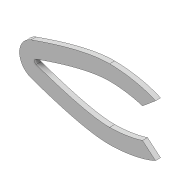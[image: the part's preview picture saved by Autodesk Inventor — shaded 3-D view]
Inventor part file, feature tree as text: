
AUTODESK INVENTOR PART (.ipt)
format: ipt  version: 2022 (Build 260153000, 153)  size: 121,856 bytes
history: native  units: mm
features: extrude x1, sketch x1
ambient origin geometry x8: Origin, YZ Plane, XZ Plane, XY Plane, X Axis, Y Axis, Z Axis, Center Point
bodies: Solid1 (feature_tree)
feature tree (2):
  extrude  "Extrusion1"  Depth=6.981317mm
  sketch  "Sketch1"  dims[d14=3.0mm d15=6.981317mm d16=6.981317mm d17=5.0mm d18=1.0mm d19=0.0mm]
